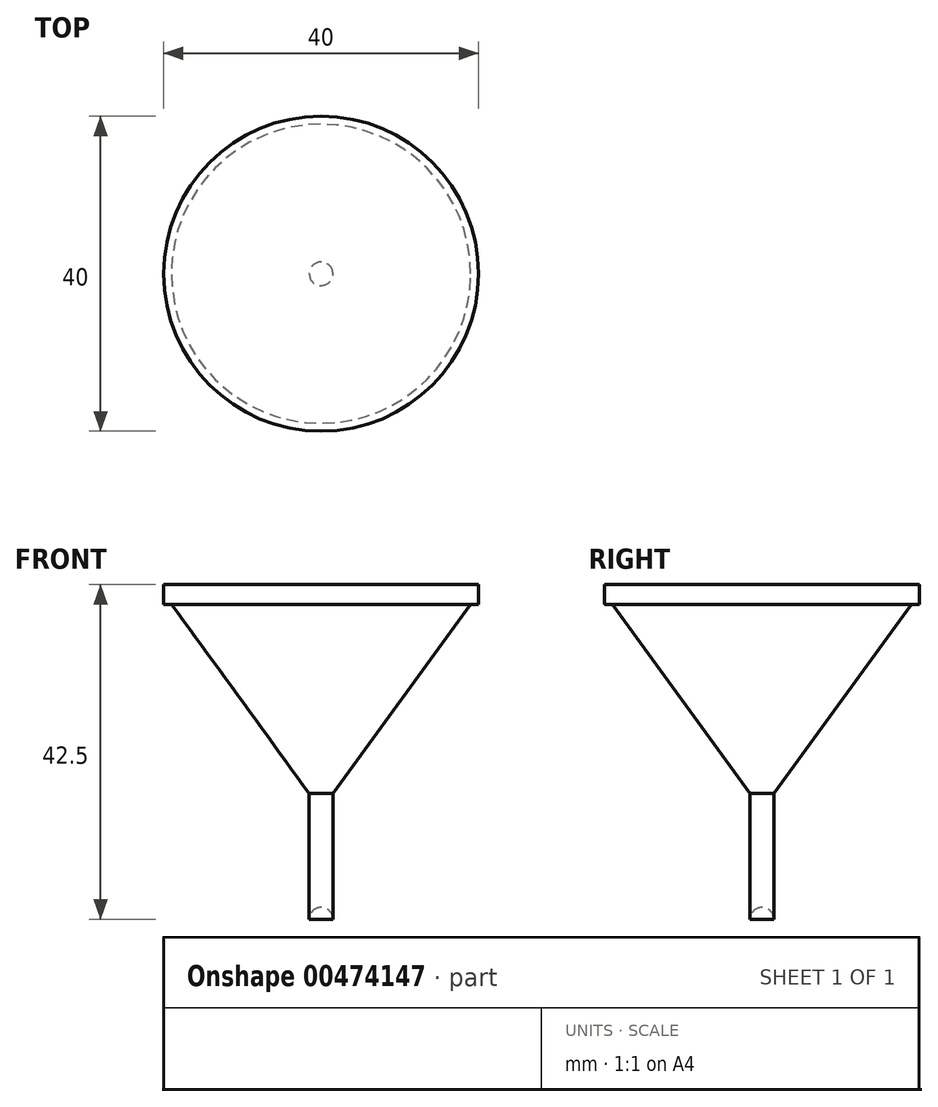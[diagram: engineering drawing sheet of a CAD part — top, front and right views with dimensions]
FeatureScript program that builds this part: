
annotation { "Feature Type Name" : "Feature", "Feature Type Description" : "" }
export const myFeature = defineFeature(function(context is Context, id is Id, definition is map)
    precondition{}
    {
        {
            var Q0;
            Q0=qCreatedBy(makeId("Front.planeOp"),FACE);
            var sketch = newSketch(context, id + "F0", { "sketchPlane" : qUnion([Q0])});
            skLineSegment(sketch, "E0.top", {"start": v(0, 40) * mm, "end": v(-1.5, 40) * mm});
            skLineSegment(sketch, "E0.left", {"start": v(0, 1.5) * mm, "end": v(0, 40) * mm});
            skLineSegment(sketch, "E0.right", {"start": v(-1.5, 0) * mm, "end": v(-1.5, 40) * mm});
            skLineSegment(sketch, "E1.bottom", {"start": v(0, 40) * mm, "end": v(-20, 40) * mm});
            skLineSegment(sketch, "E1.top", {"start": v(0, 42.5) * mm, "end": v(-20, 42.5) * mm});
            skLineSegment(sketch, "E1.left", {"start": v(0, 40) * mm, "end": v(0, 42.5) * mm});
            skLineSegment(sketch, "E1.right", {"start": v(-20, 40) * mm, "end": v(-20, 42.5) * mm});
            skArc(sketch, "E2.converted", {"start": v(0, 1.5) * mm, "mid": v(-1.06, 1.06) * mm, "end": v(-1.5, 0) * mm});
            skPoint(sketch, "E3.endSnap0", {"position": v(0, 20.75) * mm});
            skPoint(sketch, "E3.end.orphan", {"position": v(-1.5, 20.75) * mm});
            skLineSegment(sketch, "E4", {"start": v(-19, 40) * mm, "end": v(-1.5, 15.95) * mm});
            skSolve(sketch);
        }
        {
            var Q0;
            Q0 = qSketchRegion(id + "F0", true);
            var Q1;
            Q1=sQuery(id+"F0.wireOp",EDGE,"E0.left");
            revolve(context, id + "F1", {"entities" : qUnion([Q0]), "axis" : qUnion([Q1]), "revolveType" : RevolveType.FULL});
        }
    });
